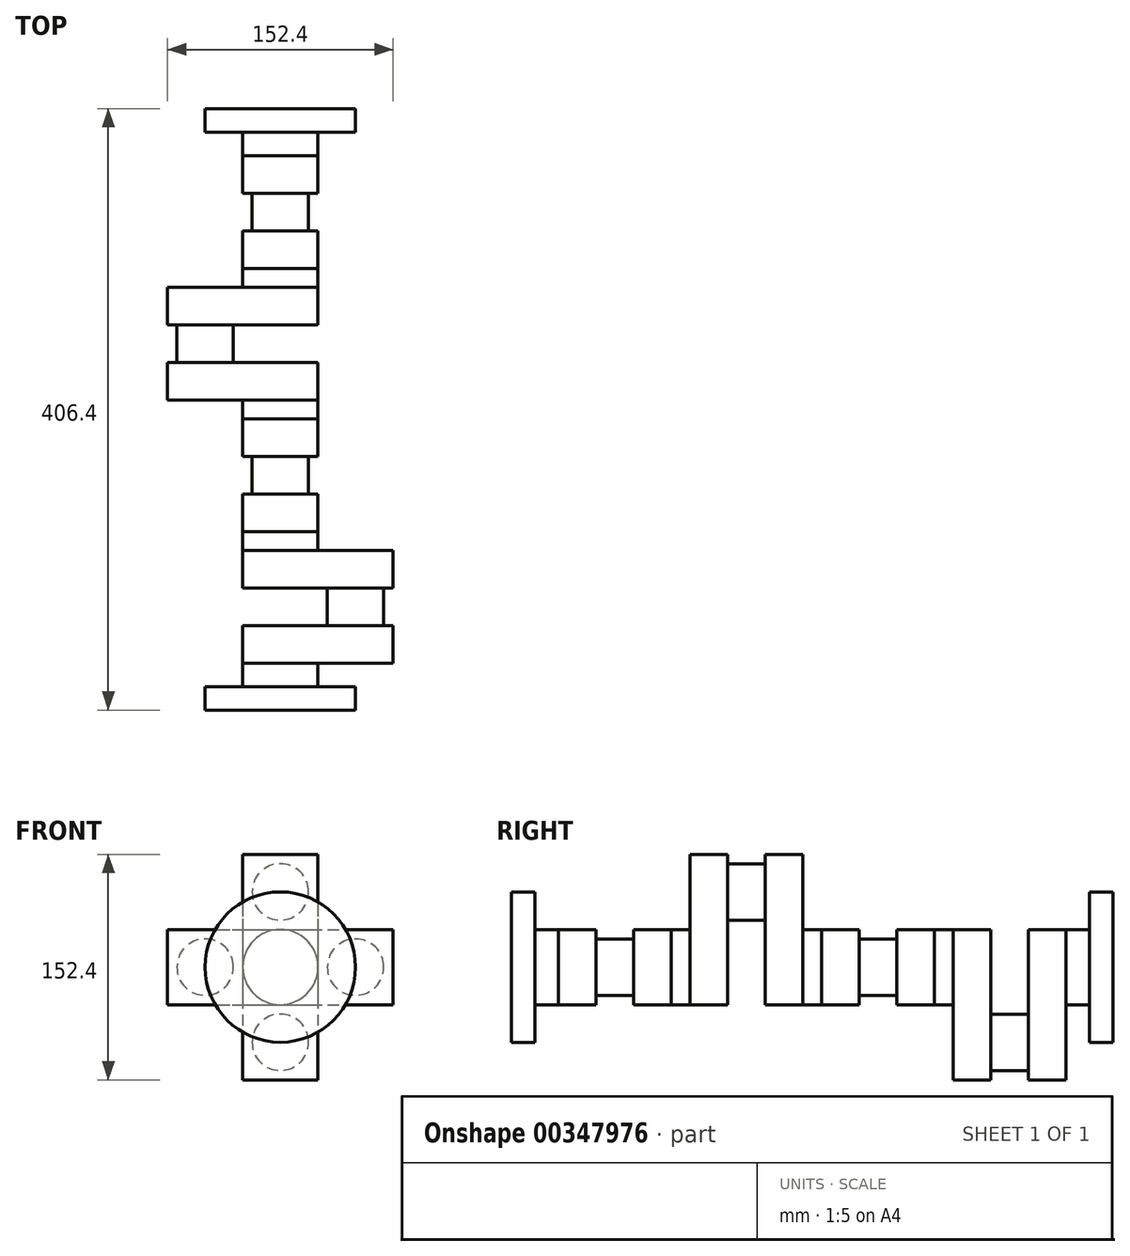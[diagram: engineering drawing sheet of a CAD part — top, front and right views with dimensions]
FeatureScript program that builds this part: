
annotation { "Feature Type Name" : "Feature", "Feature Type Description" : "" }
export const myFeature = defineFeature(function(context is Context, id is Id, definition is map)
    precondition{}
    {
        {
            var Q0;
            Q0=qCreatedBy(makeId("Front.planeOp"),FACE);
            cPlane(context, id + "F0", {"entities" : qUnion([Q0]), "cplaneType" : CPlaneType.OFFSET, "offset" : 57.15 * mm, "oppositeDirection" : true, "width" : 152.4 * mm, "height" : 152.4 * mm});
        }
        {
            var Q0;
            Q0=qCreatedBy(makeId("Front.planeOp"),FACE);
            cPlane(context, id + "F1", {"entities" : qUnion([Q0]), "cplaneType" : CPlaneType.OFFSET, "offset" : 146.05 * mm, "oppositeDirection" : true, "width" : 152.4 * mm, "height" : 152.4 * mm});
        }
        {
            var Q0;
            Q0=qCreatedBy(makeId("Front.planeOp"),FACE);
            cPlane(context, id + "F2", {"entities" : qUnion([Q0]), "cplaneType" : CPlaneType.OFFSET, "offset" : 234.95 * mm, "oppositeDirection" : true, "width" : 152.4 * mm, "height" : 152.4 * mm});
        }
        {
            var Q0;
            Q0=qCreatedBy(makeId("Front.planeOp"),FACE);
            cPlane(context, id + "F3", {"entities" : qUnion([Q0]), "cplaneType" : CPlaneType.OFFSET, "offset" : 406.4 * mm, "oppositeDirection" : true, "width" : 152.4 * mm, "height" : 152.4 * mm});
        }
        {
            var Q0;
            Q0=qCreatedBy(makeId("Front.planeOp"),FACE);
            cPlane(context, id + "F4", {"entities" : qUnion([Q0]), "cplaneType" : CPlaneType.OFFSET, "offset" : 323.85 * mm, "oppositeDirection" : true, "width" : 152.4 * mm, "height" : 152.4 * mm});
        }
        {
            var Q0;
            Q0=qCreatedBy(id+"F3.planeOp",FACE);
            var sketch = newSketch(context, id + "F5", { "sketchPlane" : qUnion([Q0])});
            skCircle(sketch, "E0", {"center": v(0, 0) * mm, "radius": 50.8 * mm});
            skSolve(sketch);
        }
        {
            var Q0;
            Q0 = qSketchRegion(id + "F5", true);
            extrude(context, id + "F6", {"entities" : qUnion([Q0]), "depth" : 15.88 * mm});
        }
        {
            var Q0;
            Q0=qCreatedBy(makeId("Front.planeOp"),FACE);
            var sketch = newSketch(context, id + "F7", { "sketchPlane" : qUnion([Q0])});
            skCircle(sketch, "E1", {"center": v(0, 0) * mm, "radius": 50.8 * mm});
            skSolve(sketch);
        }
        {
            var Q0;
            Q0 = qSketchRegion(id + "F7", true);
            extrude(context, id + "F8", {"entities" : qUnion([Q0]), "oppositeDirection" : true, "depth" : 15.88 * mm});
        }
        {
            var Q0;
            Q0=qCreatedBy(id+"F0.planeOp",FACE);
            var sketch = newSketch(context, id + "F9", { "sketchPlane" : qUnion([Q0])});
            skCircle(sketch, "E2", {"center": v(50.8, 0) * mm, "radius": 19.05 * mm});
            skSolve(sketch);
        }
        {
            var Q0;
            Q0 = qSketchRegion(id + "F9", true);
            extrude(context, id + "F10", {"entities" : qUnion([Q0]), "oppositeDirection" : true, "depth" : 25.4 * mm});
        }
        {
            var Q0;
            Q0=qCreatedBy(id+"F1.planeOp",FACE);
            var sketch = newSketch(context, id + "F11", { "sketchPlane" : qUnion([Q0])});
            skCircle(sketch, "E3", {"center": v(0, 50.8) * mm, "radius": 19.05 * mm});
            skSolve(sketch);
        }
        {
            var Q0;
            Q0 = qSketchRegion(id + "F11", true);
            extrude(context, id + "F12", {"entities" : qUnion([Q0]), "oppositeDirection" : true, "depth" : 25.4 * mm});
        }
        {
            var Q0;
            Q0=qCreatedBy(id+"F2.planeOp",FACE);
            var sketch = newSketch(context, id + "F13", { "sketchPlane" : qUnion([Q0])});
            skCircle(sketch, "E4", {"center": v(-50.8, 0) * mm, "radius": 19.05 * mm});
            skSolve(sketch);
        }
        {
            var Q0;
            Q0 = qSketchRegion(id + "F13", true);
            extrude(context, id + "F14", {"entities" : qUnion([Q0]), "oppositeDirection" : true, "depth" : 25.4 * mm});
        }
        {
            var Q0;
            Q0=qCreatedBy(id+"F4.planeOp",FACE);
            var sketch = newSketch(context, id + "F15", { "sketchPlane" : qUnion([Q0])});
            skCircle(sketch, "E5", {"center": v(0, -50.8) * mm, "radius": 19.05 * mm});
            skSolve(sketch);
        }
        {
            var Q0;
            Q0 = qSketchRegion(id + "F15", true);
            extrude(context, id + "F16", {"entities" : qUnion([Q0]), "oppositeDirection" : true, "depth" : 25.4 * mm});
        }
        {
            var Q0;
            Q0=makeQuery(id+"F16.opExtrude","CAP_FACE",FACE,{"disambiguationData":[OSD([sQuery(id+"F15.wireOp",EDGE,"E5")])],"isStart":true});
            var sketch = newSketch(context, id + "F17", { "sketchPlane" : qUnion([Q0])});
            skLineSegment(sketch, "E6.bottom", {"start": v(-25.4, 25.4) * mm, "end": v(25.4, 25.4) * mm});
            skLineSegment(sketch, "E6.top", {"start": v(-25.4, -76.2) * mm, "end": v(25.4, -76.2) * mm});
            skLineSegment(sketch, "E6.left", {"start": v(-25.4, 25.4) * mm, "end": v(-25.4, -76.2) * mm});
            skLineSegment(sketch, "E6.right", {"start": v(25.4, 25.4) * mm, "end": v(25.4, -76.2) * mm});
            skSolve(sketch);
        }
        {
            var Q0;
            Q0 = qSketchRegion(id + "F17", true);
            extrude(context, id + "F18", {"entities" : qUnion([Q0]), "operationType" : NewBodyOperationType.ADD, "depth" : 25.4 * mm});
        }
        {
            var Q0;
            Q0=makeQuery(id+"F16.opExtrude","CAP_FACE",FACE,{"disambiguationData":[OSD([sQuery(id+"F15.wireOp",EDGE,"E5")])],"isStart":false});
            var sketch = newSketch(context, id + "F19", { "sketchPlane" : qUnion([Q0])});
            skLineSegment(sketch, "E7.bottom", {"start": v(-25.4, 25.4) * mm, "end": v(25.4, 25.4) * mm});
            skLineSegment(sketch, "E7.top", {"start": v(-25.4, -76.2) * mm, "end": v(25.4, -76.2) * mm});
            skLineSegment(sketch, "E7.left", {"start": v(-25.4, 25.4) * mm, "end": v(-25.4, -76.2) * mm});
            skLineSegment(sketch, "E7.right", {"start": v(25.4, 25.4) * mm, "end": v(25.4, -76.2) * mm});
            skSolve(sketch);
        }
        {
            var Q0;
            Q0 = qSketchRegion(id + "F19", true);
            extrude(context, id + "F20", {"entities" : qUnion([Q0]), "operationType" : NewBodyOperationType.ADD, "depth" : 25.4 * mm});
        }
        {
            var Q0;
            Q0=makeQuery(id+"F14.opExtrude","CAP_FACE",FACE,{"disambiguationData":[OSD([sQuery(id+"F13.wireOp",EDGE,"E4")])],"isStart":true});
            var sketch = newSketch(context, id + "F21", { "sketchPlane" : qUnion([Q0])});
            skLineSegment(sketch, "E8.bottom", {"start": v(-76.2, 25.4) * mm, "end": v(25.4, 25.4) * mm});
            skLineSegment(sketch, "E8.top", {"start": v(-76.2, -25.4) * mm, "end": v(25.4, -25.4) * mm});
            skLineSegment(sketch, "E8.left", {"start": v(-76.2, 25.4) * mm, "end": v(-76.2, -25.4) * mm});
            skLineSegment(sketch, "E8.right", {"start": v(25.4, 25.4) * mm, "end": v(25.4, -25.4) * mm});
            skSolve(sketch);
        }
        {
            var Q0;
            Q0 = qSketchRegion(id + "F21", true);
            extrude(context, id + "F22", {"entities" : qUnion([Q0]), "operationType" : NewBodyOperationType.ADD, "depth" : 25.4 * mm});
        }
        {
            var Q0;
            Q0=makeQuery(id+"F14.opExtrude","CAP_FACE",FACE,{"disambiguationData":[OSD([sQuery(id+"F13.wireOp",EDGE,"E4")])],"isStart":false});
            var sketch = newSketch(context, id + "F23", { "sketchPlane" : qUnion([Q0])});
            skLineSegment(sketch, "E9.bottom", {"start": v(-25.4, 25.4) * mm, "end": v(76.2, 25.4) * mm});
            skLineSegment(sketch, "E9.top", {"start": v(-25.4, -25.4) * mm, "end": v(76.2, -25.4) * mm});
            skLineSegment(sketch, "E9.left", {"start": v(-25.4, 25.4) * mm, "end": v(-25.4, -25.4) * mm});
            skLineSegment(sketch, "E9.right", {"start": v(76.2, 25.4) * mm, "end": v(76.2, -25.4) * mm});
            skSolve(sketch);
        }
        {
            var Q0;
            Q0 = qSketchRegion(id + "F23", true);
            extrude(context, id + "F24", {"entities" : qUnion([Q0]), "operationType" : NewBodyOperationType.ADD, "depth" : 25.4 * mm});
        }
        {
            var Q0;
            Q0=makeQuery(id+"F12.opExtrude","CAP_FACE",FACE,{"disambiguationData":[OSD([sQuery(id+"F11.wireOp",EDGE,"E3")])],"isStart":true});
            var sketch = newSketch(context, id + "F25", { "sketchPlane" : qUnion([Q0])});
            skLineSegment(sketch, "E10.bottom", {"start": v(-25.4, 76.2) * mm, "end": v(25.4, 76.2) * mm});
            skLineSegment(sketch, "E10.top", {"start": v(-25.4, -25.4) * mm, "end": v(25.4, -25.4) * mm});
            skLineSegment(sketch, "E10.left", {"start": v(-25.4, 76.2) * mm, "end": v(-25.4, -25.4) * mm});
            skLineSegment(sketch, "E10.right", {"start": v(25.4, 76.2) * mm, "end": v(25.4, -25.4) * mm});
            skSolve(sketch);
        }
        {
            var Q0;
            Q0 = qSketchRegion(id + "F25", true);
            extrude(context, id + "F26", {"entities" : qUnion([Q0]), "operationType" : NewBodyOperationType.ADD, "depth" : 25.4 * mm});
        }
        {
            var Q0;
            Q0=makeQuery(id+"F12.opExtrude","CAP_FACE",FACE,{"disambiguationData":[OSD([sQuery(id+"F11.wireOp",EDGE,"E3")])],"isStart":false});
            var sketch = newSketch(context, id + "F27", { "sketchPlane" : qUnion([Q0])});
            skLineSegment(sketch, "E11.bottom", {"start": v(-25.4, 76.2) * mm, "end": v(25.4, 76.2) * mm});
            skLineSegment(sketch, "E11.top", {"start": v(-25.4, -25.4) * mm, "end": v(25.4, -25.4) * mm});
            skLineSegment(sketch, "E11.left", {"start": v(-25.4, 76.2) * mm, "end": v(-25.4, -25.4) * mm});
            skLineSegment(sketch, "E11.right", {"start": v(25.4, 76.2) * mm, "end": v(25.4, -25.4) * mm});
            skSolve(sketch);
        }
        {
            var Q0;
            Q0 = qSketchRegion(id + "F27", true);
            extrude(context, id + "F28", {"entities" : qUnion([Q0]), "operationType" : NewBodyOperationType.ADD, "depth" : 25.4 * mm});
        }
        {
            var Q0;
            Q0=makeQuery(id+"F10.opExtrude","CAP_FACE",FACE,{"disambiguationData":[OSD([sQuery(id+"F9.wireOp",EDGE,"E2")])],"isStart":true});
            var sketch = newSketch(context, id + "F29", { "sketchPlane" : qUnion([Q0])});
            skLineSegment(sketch, "E12.bottom", {"start": v(-25.4, 25.4) * mm, "end": v(76.2, 25.4) * mm});
            skLineSegment(sketch, "E12.top", {"start": v(-25.4, -25.4) * mm, "end": v(76.2, -25.4) * mm});
            skLineSegment(sketch, "E12.left", {"start": v(-25.4, 25.4) * mm, "end": v(-25.4, -25.4) * mm});
            skLineSegment(sketch, "E12.right", {"start": v(76.2, 25.4) * mm, "end": v(76.2, -25.4) * mm});
            skSolve(sketch);
        }
        {
            var Q0;
            Q0 = qSketchRegion(id + "F29", true);
            extrude(context, id + "F30", {"entities" : qUnion([Q0]), "operationType" : NewBodyOperationType.ADD, "depth" : 25.4 * mm});
        }
        {
            var Q0;
            Q0=makeQuery(id+"F10.opExtrude","CAP_FACE",FACE,{"disambiguationData":[OSD([sQuery(id+"F9.wireOp",EDGE,"E2")])],"isStart":false});
            var sketch = newSketch(context, id + "F31", { "sketchPlane" : qUnion([Q0])});
            skLineSegment(sketch, "E13.bottom", {"start": v(-76.2, -25.4) * mm, "end": v(25.4, -25.4) * mm});
            skLineSegment(sketch, "E13.top", {"start": v(-76.2, 25.4) * mm, "end": v(25.4, 25.4) * mm});
            skLineSegment(sketch, "E13.left", {"start": v(-76.2, -25.4) * mm, "end": v(-76.2, 25.4) * mm});
            skLineSegment(sketch, "E13.right", {"start": v(25.4, -25.4) * mm, "end": v(25.4, 25.4) * mm});
            skSolve(sketch);
        }
        {
            var Q0;
            Q0 = qSketchRegion(id + "F31", true);
            extrude(context, id + "F32", {"entities" : qUnion([Q0]), "operationType" : NewBodyOperationType.ADD, "depth" : 25.4 * mm});
        }
        {
            var Q0;
            Q0=makeQuery(id+"F8.opExtrude","CAP_FACE",FACE,{"disambiguationData":[OSD([sQuery(id+"F7.wireOp",EDGE,"E1")])],"isStart":false});
            var sketch = newSketch(context, id + "F33", { "sketchPlane" : qUnion([Q0])});
            skCircle(sketch, "E14", {"center": v(0, 0) * mm, "radius": 25.4 * mm});
            skSolve(sketch);
        }
        {
            var Q0;
            Q0 = qSketchRegion(id + "F33", true);
            var Q1;
            Q1=makeQuery(id+"F30.opExtrude","CAP_FACE",FACE,{"disambiguationData":[OSD([sQuery(id+"F29.wireOp",EDGE,"E12.bottom"),sQuery(id+"F29.wireOp",EDGE,"E12.top"),sQuery(id+"F29.wireOp",EDGE,"E12.left"),sQuery(id+"F29.wireOp",EDGE,"E12.right")])],"isStart":false});
            extrude(context, id + "F34", {"entities" : qUnion([Q0]), "endBound" : BoundingType.UP_TO_SURFACE, "endBoundEntityFace" : qUnion([Q1]), "depth" : 25.4 * mm});
        }
        {
            var Q0;
            Q0=makeQuery(id+"F26.opExtrude","CAP_FACE",FACE,{"disambiguationData":[OSD([sQuery(id+"F25.wireOp",EDGE,"E10.bottom"),sQuery(id+"F25.wireOp",EDGE,"E10.top"),sQuery(id+"F25.wireOp",EDGE,"E10.left"),sQuery(id+"F25.wireOp",EDGE,"E10.right")])],"isStart":false});
            var sketch = newSketch(context, id + "F35", { "sketchPlane" : qUnion([Q0])});
            skCircle(sketch, "E15", {"center": v(0, 0) * mm, "radius": 25.4 * mm});
            skSolve(sketch);
        }
        {
            var Q0;
            Q0 = qSketchRegion(id + "F35", true);
            var Q1;
            Q1=makeQuery(id+"F32.opExtrude","CAP_FACE",FACE,{"disambiguationData":[OSD([sQuery(id+"F31.wireOp",EDGE,"E13.bottom"),sQuery(id+"F31.wireOp",EDGE,"E13.top"),sQuery(id+"F31.wireOp",EDGE,"E13.left"),sQuery(id+"F31.wireOp",EDGE,"E13.right")])],"isStart":false});
            extrude(context, id + "F36", {"entities" : qUnion([Q0]), "endBound" : BoundingType.UP_TO_SURFACE, "endBoundEntityFace" : qUnion([Q1]), "depth" : 25.4 * mm});
        }
        {
            var Q0;
            Q0=makeQuery(id+"F22.opExtrude","CAP_FACE",FACE,{"disambiguationData":[OSD([sQuery(id+"F21.wireOp",EDGE,"E8.bottom"),sQuery(id+"F21.wireOp",EDGE,"E8.top"),sQuery(id+"F21.wireOp",EDGE,"E8.left"),sQuery(id+"F21.wireOp",EDGE,"E8.right")])],"isStart":false});
            var sketch = newSketch(context, id + "F37", { "sketchPlane" : qUnion([Q0])});
            skCircle(sketch, "E16", {"center": v(0, 0) * mm, "radius": 25.4 * mm});
            skSolve(sketch);
        }
        {
            var Q0;
            Q0 = qSketchRegion(id + "F37", true);
            var Q1;
            Q1=makeQuery(id+"F28.opExtrude","CAP_FACE",FACE,{"disambiguationData":[OSD([sQuery(id+"F27.wireOp",EDGE,"E11.bottom"),sQuery(id+"F27.wireOp",EDGE,"E11.top"),sQuery(id+"F27.wireOp",EDGE,"E11.left"),sQuery(id+"F27.wireOp",EDGE,"E11.right")])],"isStart":false});
            extrude(context, id + "F38", {"entities" : qUnion([Q0]), "endBound" : BoundingType.UP_TO_SURFACE, "endBoundEntityFace" : qUnion([Q1]), "depth" : 25.4 * mm});
        }
        {
            var Q0;
            Q0=makeQuery(id+"F18.opExtrude","CAP_FACE",FACE,{"disambiguationData":[OSD([sQuery(id+"F17.wireOp",EDGE,"E6.bottom"),sQuery(id+"F17.wireOp",EDGE,"E6.top"),sQuery(id+"F17.wireOp",EDGE,"E6.left"),sQuery(id+"F17.wireOp",EDGE,"E6.right")])],"isStart":false});
            var sketch = newSketch(context, id + "F39", { "sketchPlane" : qUnion([Q0])});
            skCircle(sketch, "E17", {"center": v(0, 0) * mm, "radius": 25.4 * mm});
            skSolve(sketch);
        }
        {
            var Q0;
            Q0 = qSketchRegion(id + "F39", true);
            var Q1;
            Q1=makeQuery(id+"F24.opExtrude","CAP_FACE",FACE,{"disambiguationData":[OSD([sQuery(id+"F23.wireOp",EDGE,"E9.bottom"),sQuery(id+"F23.wireOp",EDGE,"E9.top"),sQuery(id+"F23.wireOp",EDGE,"E9.left"),sQuery(id+"F23.wireOp",EDGE,"E9.right")])],"isStart":false});
            extrude(context, id + "F40", {"entities" : qUnion([Q0]), "endBound" : BoundingType.UP_TO_SURFACE, "endBoundEntityFace" : qUnion([Q1]), "depth" : 25.4 * mm});
        }
        {
            var Q0;
            Q0=makeQuery(id+"F6.opExtrude","CAP_FACE",FACE,{"disambiguationData":[OSD([sQuery(id+"F5.wireOp",EDGE,"E0")])],"isStart":false});
            var sketch = newSketch(context, id + "F41", { "sketchPlane" : qUnion([Q0])});
            skCircle(sketch, "E18", {"center": v(0, 0) * mm, "radius": 25.4 * mm});
            skSolve(sketch);
        }
        {
            var Q0;
            Q0 = qSketchRegion(id + "F41", true);
            var Q1;
            Q1=makeQuery(id+"F20.opExtrude","CAP_FACE",FACE,{"disambiguationData":[OSD([sQuery(id+"F19.wireOp",EDGE,"E7.bottom"),sQuery(id+"F19.wireOp",EDGE,"E7.top"),sQuery(id+"F19.wireOp",EDGE,"E7.left"),sQuery(id+"F19.wireOp",EDGE,"E7.right")])],"isStart":false});
            extrude(context, id + "F42", {"entities" : qUnion([Q0]), "endBound" : BoundingType.UP_TO_SURFACE, "endBoundEntityFace" : qUnion([Q1]), "depth" : 25.4 * mm});
        }
    });
